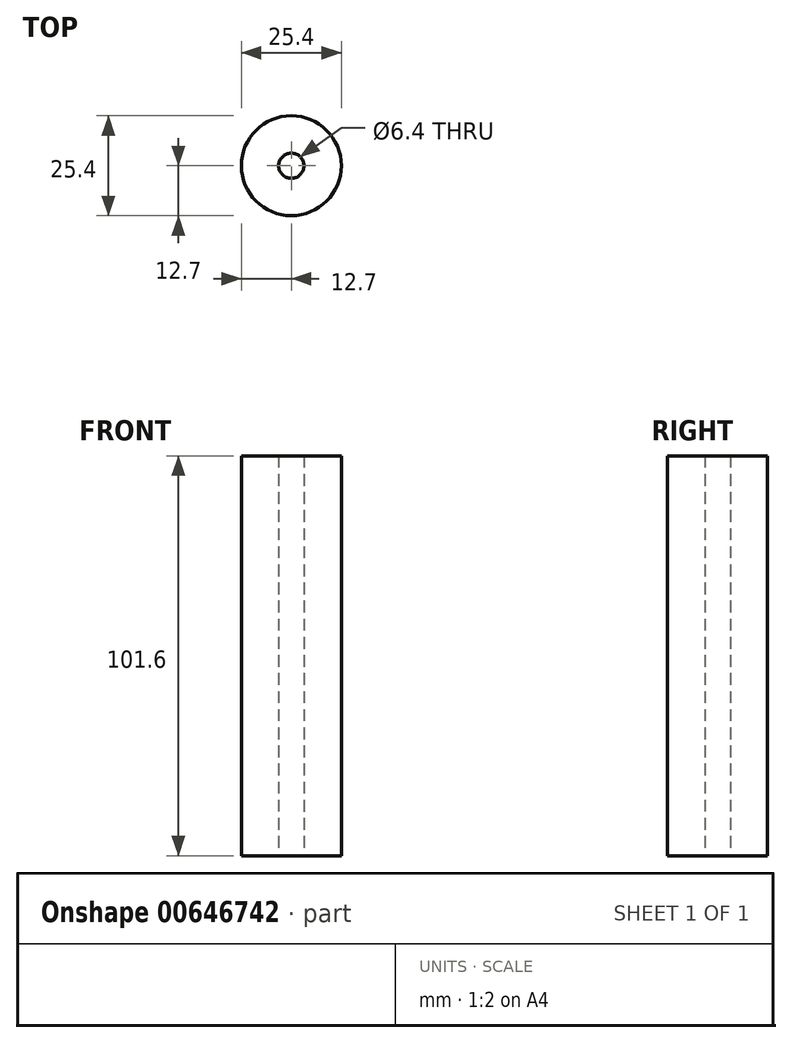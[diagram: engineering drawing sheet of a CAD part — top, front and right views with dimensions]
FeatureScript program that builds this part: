
annotation { "Feature Type Name" : "Feature", "Feature Type Description" : "" }
export const myFeature = defineFeature(function(context is Context, id is Id, definition is map)
    precondition{}
    {
        {
            var Q0;
            Q0=qCreatedBy(makeId("Top.planeOp"),FACE);
            var sketch = newSketch(context, id + "F0", { "sketchPlane" : qUnion([Q0])});
            skCircle(sketch, "E0", {"center": v(0, 0) * mm, "radius": 12.7 * mm});
            skCircle(sketch, "E1", {"center": v(0, 0) * mm, "radius": 3.2 * mm});
            skSolve(sketch);
        }
        {
            var Q0;
            Q0=makeQuery(id+"F0.imprint","IMPRINT",FACE,{"disambiguationData":[TD([[makeQuery(id+"F0.imprint","IMPRINT",EDGE,{"derivedFrom":sQuery(id+"F0.wireOp",EDGE,"E0")}),1.0]])]});
            extrude(context, id + "F1", {"entities" : qUnion([Q0]), "depth" : 101.6 * mm, "offsetDistance" : 25.4 * mm});
        }
    });
